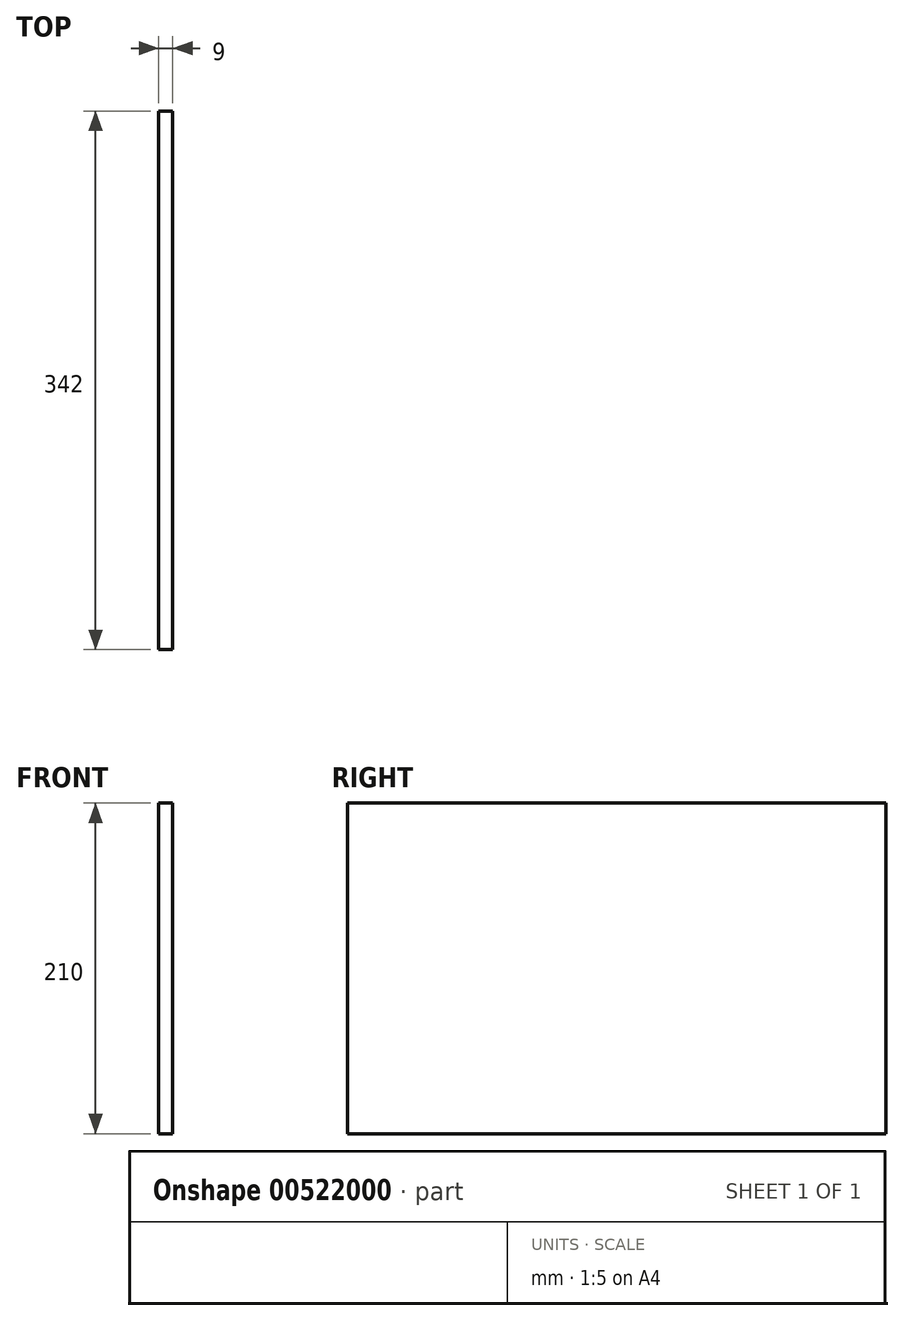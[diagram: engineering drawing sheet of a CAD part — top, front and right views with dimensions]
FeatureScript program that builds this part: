
annotation { "Feature Type Name" : "Feature", "Feature Type Description" : "" }
export const myFeature = defineFeature(function(context is Context, id is Id, definition is map)
    precondition{}
    {
        {
            var Q0;
            Q0=qCreatedBy(makeId("Right.planeOp"),FACE);
            var sketch = newSketch(context, id + "F0", { "sketchPlane" : qUnion([Q0])});
            skLineSegment(sketch, "E0.bottom", {"start": v(0, 0) * mm, "end": v(-342, 0) * mm});
            skLineSegment(sketch, "E0.top", {"start": v(0, 210) * mm, "end": v(-342, 210) * mm});
            skLineSegment(sketch, "E0.left", {"start": v(0, 0) * mm, "end": v(0, 210) * mm});
            skLineSegment(sketch, "E0.right", {"start": v(-342, 0) * mm, "end": v(-342, 210) * mm});
            skSolve(sketch);
        }
        {
            var Q0;
            Q0=makeQuery(id+"F0.imprint","IMPRINT",FACE,{"disambiguationData":[TD([[makeQuery(id+"F0.imprint","IMPRINT",EDGE,{"derivedFrom":sQuery(id+"F0.wireOp",EDGE,"E0.bottom")}),-1.0]])]});
            extrude(context, id + "F1", {"entities" : qUnion([Q0]), "depth" : 9 * mm, "offsetDistance" : 25 * mm});
        }
    });
